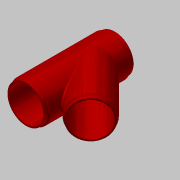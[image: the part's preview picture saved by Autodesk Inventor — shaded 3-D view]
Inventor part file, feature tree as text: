
AUTODESK INVENTOR PART (.ipt)
format: ipt  version: 2017.3 (Build 213257000, 257)  size: 291,328 bytes
history: native  units: in
note: dims shown in document units (in); Inventor stores cm internally (conversion verified against a paired STEP export)
features: extrude x18, sketch x14, fillet x6, chamfer x3, plane x1
ambient origin geometry x8: Origin, YZ Plane, XZ Plane, XY Plane, X Axis, Y Axis, Z Axis, Center Point
bodies: Solid1 (feature_tree)
feature tree (42):
  sketch  "Sketch1"  dims[d0=28.5in d1=31.0in]
  extrude  "Extrusion1"  Depth=31.0in
  plane  "Work Plane1"
  sketch  "Sketch2"  dims[d2=33.0in d3=52.9606in d4=19.4961in d5=0.0in d6=0.0in]
  extrude  "Extrusion2"  Depth=52.9606in TaperAngle=0.0deg
  extrude  "Extrusion3"  Depth=28.5in
  extrude  "Extrusion4"  Depth=33.0in
  extrude  "Extrusion5"  Depth=30.0in
  extrude  "Extrusion6"  Depth=30.0in
  extrude  "Extrusion7"  TaperAngle=0.0deg  [1 undecoded]
  extrude  "Extrusion8"  Depth=0.5in
  extrude  "Extrusion9"  Depth=49.9606in
  fillet  "Fillet1"  Radius=16.4961in
  fillet  "Fillet2"  [1 undecoded]
  fillet  "Fillet3"  Radius=49.9606in
  fillet  "Fillet4"  [1 undecoded]
  extrude  "Extrusion10"  TaperAngle=0.0deg  [1 undecoded]
  extrude  "Extrusion11"  TaperAngle=0.0deg  [1 undecoded]
  extrude  "Extrusion12"  Depth=6.0in
  fillet  "Fillet5"  Radius=1.0in
  chamfer  "Chamfer2"  Distance=1.0in
  fillet  "Fillet6"  Radius=32.48in
  chamfer  "Chamfer3"  Distance=1.0in
  extrude  "Extrusion13"  Depth=32.48in
  extrude  "Extrusion14"  Depth=1.0in TaperAngle=0.0deg
  extrude  "Extrusion15"  Depth=0.0312in
  chamfer  "Chamfer4"  Distance=0.74in
  extrude  "Extrusion16"  Depth=0.125in TaperAngle=45.0deg
  extrude  "Extrusion17"  Depth=0.0312in
  extrude  "Extrusion18"  Depth=0.0312in TaperAngle=45.0deg
  sketch  "Sketch3"  dims[d7=45.0deg d8=28.5in]
  sketch  "Sketch4"  dims[d9=31.0in d10=33.0in]
  sketch  "Sketch5"  dims[d11=52.9606in d12=0.0in d13=30.0in]
  sketch  "Sketch6"  dims[d14=0.5in d15=0.0in d16=30.0in]
  sketch  "Sketch7"  dims[d17=0.5in d18=0.0in]
  sketch  "Sketch8"  dims[d19=30.0in d20=0.5in]
  sketch  "Sketch9"  dims[d21=0.0in d22=49.9606in d23=16.4961in d24=0.0in d25=0.0in d26=49.9606in d27=0.0in]
  sketch  "Sketch10"  dims[d28=52.9606in d29=0.0in]
  sketch  "Sketch11"  dims[d30=52.9606in d31=0.0in]
  sketch  "Sketch12"  dims[d32=1.0in d33=6.0in d34=1.0in]
  sketch  "Sketch13"  dims[d35=1.0in]
  sketch  "Sketch14"  dims[d39=32.48in d40=1.0in d41=0.0in d42=32.48in d43=1.0in d44=0.0in d45=32.48in d46=1.0in d47=0.0in d48=0.0312in d49=0.74in d50=0.125in d51=45.0deg d52=0.0312in d53=0.0312in d54=0.125in d55=45.0deg d56=1.0in d57=0.0in d58=1.0in d59=0.0in d60=1.0in d61=0.0in d62=0.26in d64=0.125in d65=45.0deg d66=1.0in d67=0.0in d68=1.0in d69=0.0in d70=1.0in d71=0.0in]
note: 5 required parameter values undecoded (feature->parameter linkage not recoverable at this tier; creation-order binding heuristic only, values carry confidence <= 0.55)
